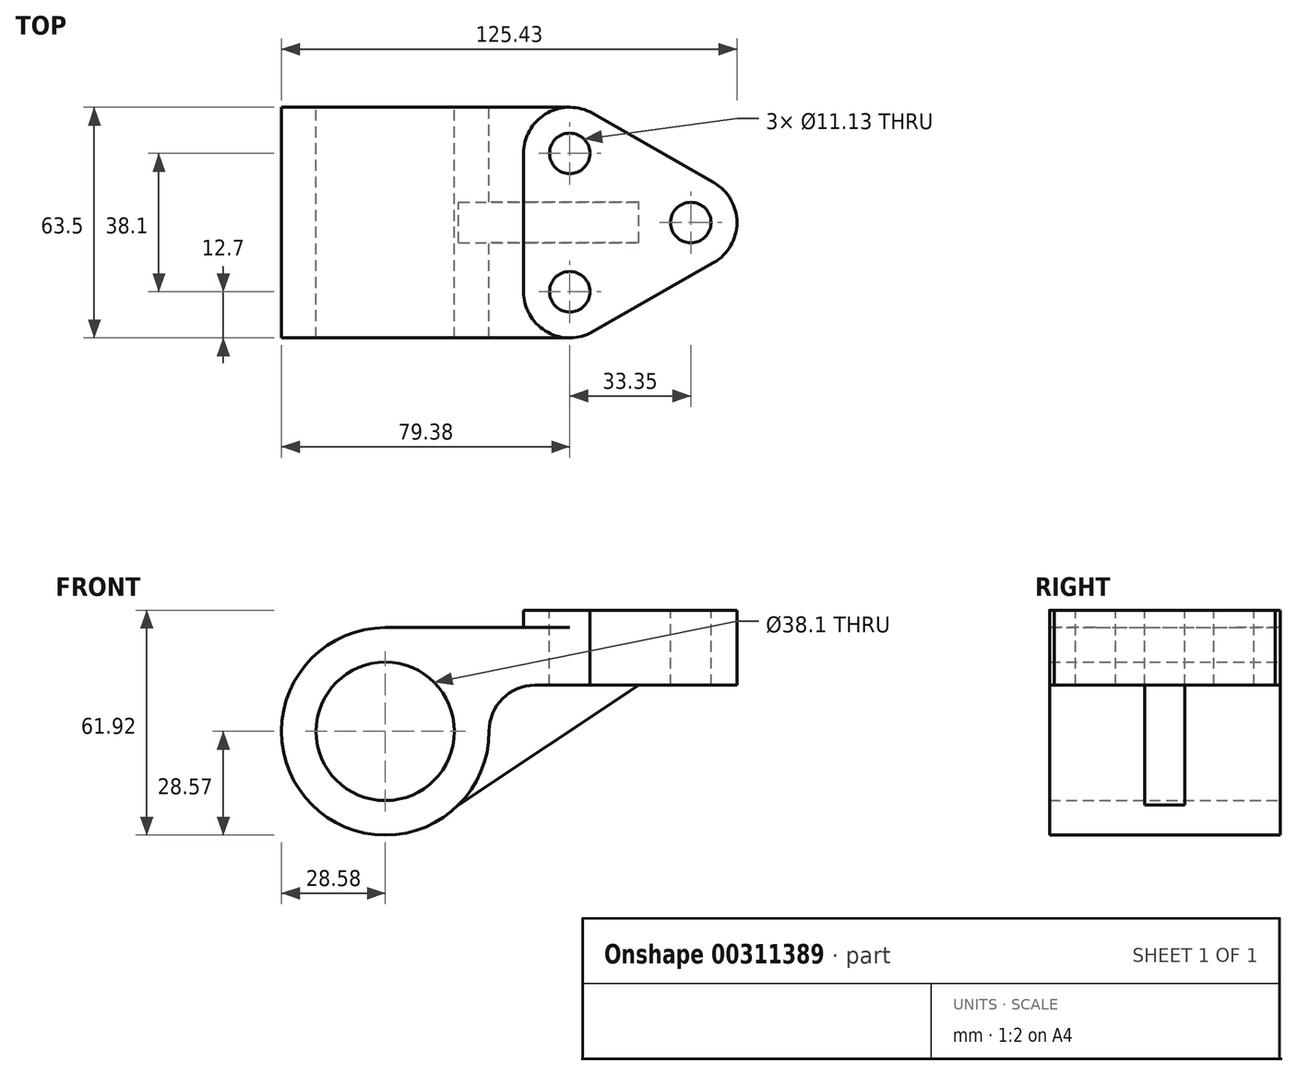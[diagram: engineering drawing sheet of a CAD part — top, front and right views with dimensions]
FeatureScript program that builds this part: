
annotation { "Feature Type Name" : "Feature", "Feature Type Description" : "" }
export const myFeature = defineFeature(function(context is Context, id is Id, definition is map)
    precondition{}
    {
        {
            var Q0;
            Q0=qCreatedBy(makeId("Front.planeOp"),FACE);
            var sketch = newSketch(context, id + "F0", { "sketchPlane" : qUnion([Q0])});
            skCircle(sketch, "E0", {"center": v(0, 0) * mm, "radius": 19.05 * mm});
            skArc(sketch, "E1", {"start": v(0, 28.58) * mm, "mid": v(-20.2, -20.2) * mm, "end": v(28.58, 0) * mm});
            skLineSegment(sketch, "E2", {"start": v(0, 28.58) * mm, "end": v(50.8, 28.58) * mm});
            skLineSegment(sketch, "E3", {"start": v(38.1, 33.35) * mm, "end": v(96.85, 33.35) * mm});
            skLineSegment(sketch, "E4", {"start": v(96.85, 12.7) * mm, "end": v(41.27, 12.7) * mm});
            skPoint(sketch, "E5", {"position": v(69.85, 12.7) * mm});
            skLineSegment(sketch, "E6", {"start": v(38.1, 33.35) * mm, "end": v(38.1, 28.58) * mm});
            skLineSegment(sketch, "E7", {"start": v(96.85, 33.35) * mm, "end": v(96.85, 12.7) * mm});
            skArc(sketch, "E8", {"start": v(41.27, 12.7) * mm, "mid": v(32.3, 8.98) * mm, "end": v(28.57, 0) * mm});
            skArc(sketch, "E9", {"start": v(0, -28.58) * mm, "mid": v(20.2, -20.2) * mm, "end": v(28.58, 0) * mm});
            skPoint(sketch, "E10", {"position": v(20.2, -20.2) * mm});
            skLineSegment(sketch, "E11", {"start": v(20.2, -20.2) * mm, "end": v(69.85, 12.7) * mm});
            skSolve(sketch);
        }
        {
            var Q0;
            Q0=makeQuery(id+"F0.imprint","IMPRINT",FACE,{"disambiguationData":[TD([[makeQuery(id+"F0.imprint","IMPRINT",EDGE,{"derivedFrom":sQuery(id+"F0.wireOp",EDGE,"E0")}),-1.0]])]});
            extrude(context, id + "F1", {"entities" : qUnion([Q0]), "endBound" : BoundingType.SYMMETRIC, "depth" : 63.5 * mm});
        }
        {
            var Q0;
            Q0=makeQuery(id+"F1.opExtrude","SWEPT_FACE",FACE,{"disambiguationData":[OSD([sQuery(id+"F0.wireOp",EDGE,"E3")])]});
            var sketch = newSketch(context, id + "F2", { "sketchPlane" : qUnion([Q0])});
            skLineSegment(sketch, "E12", {"start": v(96.85, 0) * mm, "end": v(-28.58, 0) * mm, "construction": true});
            skPoint(sketch, "E12.endSnap0", {"position": v(96.85, 0) * mm});
            skPoint(sketch, "E13", {"position": v(38.1, 0) * mm});
            skPoint(sketch, "E14", {"position": v(84.15, 0) * mm});
            skCircle(sketch, "E15", {"center": v(84.15, 0) * mm, "radius": 5.56 * mm});
            skLineSegment(sketch, "E16", {"start": v(38.1, 19.05) * mm, "end": v(38.1, -19.05) * mm});
            skCircle(sketch, "E17", {"center": v(50.8, 19.05) * mm, "radius": 5.56 * mm});
            skCircle(sketch, "E18", {"center": v(50.8, -19.05) * mm, "radius": 5.56 * mm});
            skPoint(sketch, "E19", {"position": v(56.36, -19.05) * mm});
            skPoint(sketch, "E20", {"position": v(56.36, 19.05) * mm});
            skLineSegment(sketch, "E21", {"start": v(50.8, 19.05) * mm, "end": v(84.15, 0) * mm, "construction": true});
            skLineSegment(sketch, "E22", {"start": v(50.8, -19.05) * mm, "end": v(84.15, 0) * mm, "construction": true});
            skLineSegment(sketch, "E23", {"start": v(50.8, 19.05) * mm, "end": v(50.8, -19.05) * mm, "construction": true});
            skArc(sketch, "E24", {"start": v(38.1, 19.05) * mm, "mid": v(44.07, 29.82) * mm, "end": v(56.36, 30.47) * mm});
            skArc(sketch, "E25", {"start": v(38.1, -19.05) * mm, "mid": v(44.07, -29.82) * mm, "end": v(56.36, -30.47) * mm});
            skArc(sketch, "E26", {"start": v(90.44, 11.03) * mm, "mid": v(96.85, 0) * mm, "end": v(90.44, -11.03) * mm});
            skLineSegment(sketch, "E27", {"start": v(56.36, 30.47) * mm, "end": v(90.44, 11.03) * mm});
            skLineSegment(sketch, "E28", {"start": v(56.36, -30.47) * mm, "end": v(90.44, -11.03) * mm});
            skLineSegment(sketch, "E29", {"start": v(38.1, 19.05) * mm, "end": v(38.1, 31.75) * mm});
            skLineSegment(sketch, "E30", {"start": v(38.1, 31.75) * mm, "end": v(56.36, 31.75) * mm});
            skLineSegment(sketch, "E31", {"start": v(56.36, 31.75) * mm, "end": v(56.36, 30.47) * mm});
            skLineSegment(sketch, "E32", {"start": v(38.1, -19.05) * mm, "end": v(38.1, -31.75) * mm});
            skLineSegment(sketch, "E33", {"start": v(38.1, -31.75) * mm, "end": v(56.36, -31.75) * mm});
            skLineSegment(sketch, "E34", {"start": v(56.36, -31.75) * mm, "end": v(56.36, -30.47) * mm});
            skSolve(sketch);
        }
        {
            var Q0;
            Q0=makeQuery(id+"F2.imprint","IMPRINT",FACE,{"disambiguationData":[TD([[makeQuery(id+"F2.imprint","IMPRINT",EDGE,{"derivedFrom":sQuery(id+"F2.wireOp",EDGE,"E17")}),1.0]])]});
            var Q1;
            Q1=makeQuery(id+"F2.imprint","IMPRINT",FACE,{"disambiguationData":[TD([[makeQuery(id+"F2.imprint","IMPRINT",EDGE,{"derivedFrom":sQuery(id+"F2.wireOp",EDGE,"E18")}),1.0]])]});
            var Q2;
            Q2=makeQuery(id+"F2.imprint","IMPRINT",FACE,{"disambiguationData":[TD([[makeQuery(id+"F2.imprint","IMPRINT",EDGE,{"derivedFrom":sQuery(id+"F2.wireOp",EDGE,"E15")}),1.0]])]});
            extrude(context, id + "F3", {"entities" : qUnion([Q0, Q1, Q2]), "operationType" : NewBodyOperationType.REMOVE, "endBound" : BoundingType.THROUGH_ALL, "oppositeDirection" : true, "depth" : 25.4 * mm});
        }
        {
            var Q0;
            {var subQ0=sQuery(id+"F2.wireOp",EDGE,"E29");Q0=makeQuery(id+"F2.imprint","IMPRINT",FACE,{"disambiguationData":[TD([[makeQuery(id+"F2.imprint","IMPRINT",EDGE,{"derivedFrom":subQ0}),-1.0]])]});}
            var Q1;
            {var subQ0=sQuery(id+"F2.wireOp",EDGE,"E32");Q1=makeQuery(id+"F2.imprint","IMPRINT",FACE,{"disambiguationData":[TD([[makeQuery(id+"F2.imprint","IMPRINT",EDGE,{"derivedFrom":subQ0}),-1.0]])]});}
            extrude(context, id + "F4", {"entities" : qUnion([Q0, Q1]), "operationType" : NewBodyOperationType.REMOVE, "oppositeDirection" : true, "depth" : 4.78 * mm});
        }
        {
            var Q0;
            {var subQ5=sQuery(id+"F2.wireOp",EDGE,"E27");Q0=makeQuery(id+"F2.imprint","IMPRINT",FACE,{"disambiguationData":[TD([[makeQuery(id+"F2.imprint","IMPRINT",EDGE,{"derivedFrom":subQ5}),1.0]])]});}
            var Q1;
            {var subQ5=sQuery(id+"F2.wireOp",EDGE,"E28");Q1=makeQuery(id+"F2.imprint","IMPRINT",FACE,{"disambiguationData":[TD([[makeQuery(id+"F2.imprint","IMPRINT",EDGE,{"derivedFrom":subQ5}),-1.0]])]});}
            var Q2;
            {var subQ0=sQuery(id+"F2.wireOp",EDGE,"E34");Q2=makeQuery(id+"F2.imprint","IMPRINT",FACE,{"disambiguationData":[TD([[makeQuery(id+"F2.imprint","IMPRINT",EDGE,{"derivedFrom":subQ0}),1.0]])]});}
            var Q3;
            {var subQ0=sQuery(id+"F2.wireOp",EDGE,"E31");Q3=makeQuery(id+"F2.imprint","IMPRINT",FACE,{"disambiguationData":[TD([[makeQuery(id+"F2.imprint","IMPRINT",EDGE,{"derivedFrom":subQ0}),-1.0]])]});}
            extrude(context, id + "F5", {"entities" : qUnion([Q0, Q1, Q2, Q3]), "operationType" : NewBodyOperationType.REMOVE, "endBound" : BoundingType.THROUGH_ALL, "oppositeDirection" : true, "depth" : 20.65 * mm});
        }
        {
            var Q0;
            {var subQ0=sQuery(id+"F0.wireOp",EDGE,"E8");Q0=makeQuery(id+"F0.imprint","IMPRINT",FACE,{"disambiguationData":[TD([[makeQuery(id+"F0.imprint","IMPRINT",EDGE,{"derivedFrom":subQ0}),1.0]])]});}
            extrude(context, id + "F6", {"entities" : qUnion([Q0]), "operationType" : NewBodyOperationType.ADD, "endBound" : BoundingType.SYMMETRIC, "depth" : 11.13 * mm});
        }
    });
